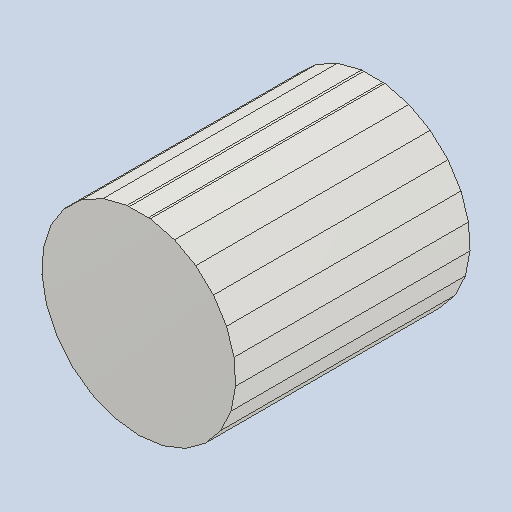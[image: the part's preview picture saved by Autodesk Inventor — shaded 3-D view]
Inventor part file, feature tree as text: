
AUTODESK INVENTOR PART (.ipt)
format: ipt  version: 2024 (Build 280153000, 153)  size: 152,064 bytes
history: native  units: mm (DEFAULTED — no unit token found)
features: other x3, extrude x2, fillet x1, pattern_circular x1
ambient origin geometry x8: Origin, YZ Plane, XZ Plane, XY Plane, X Axis, Y Axis, Z Axis, Center Point
bodies: Solid1 (feature_tree)
feature tree (7):
  other  "Pulley Sketch"
  extrude  "Base Body"  Depth=19.894368mm
  extrude  "Tooth"  Depth=0.3mm
  fillet  "Tooth Fillet"  Radius=2.67mm
  pattern_circular  "Teeth"  [2 undecoded]
  other  "Left flange"
  other  "Right flange"
note: 2 required parameter values undecoded (feature->parameter linkage not recoverable at this tier; creation-order binding heuristic only, values carry confidence <= 0.55)
